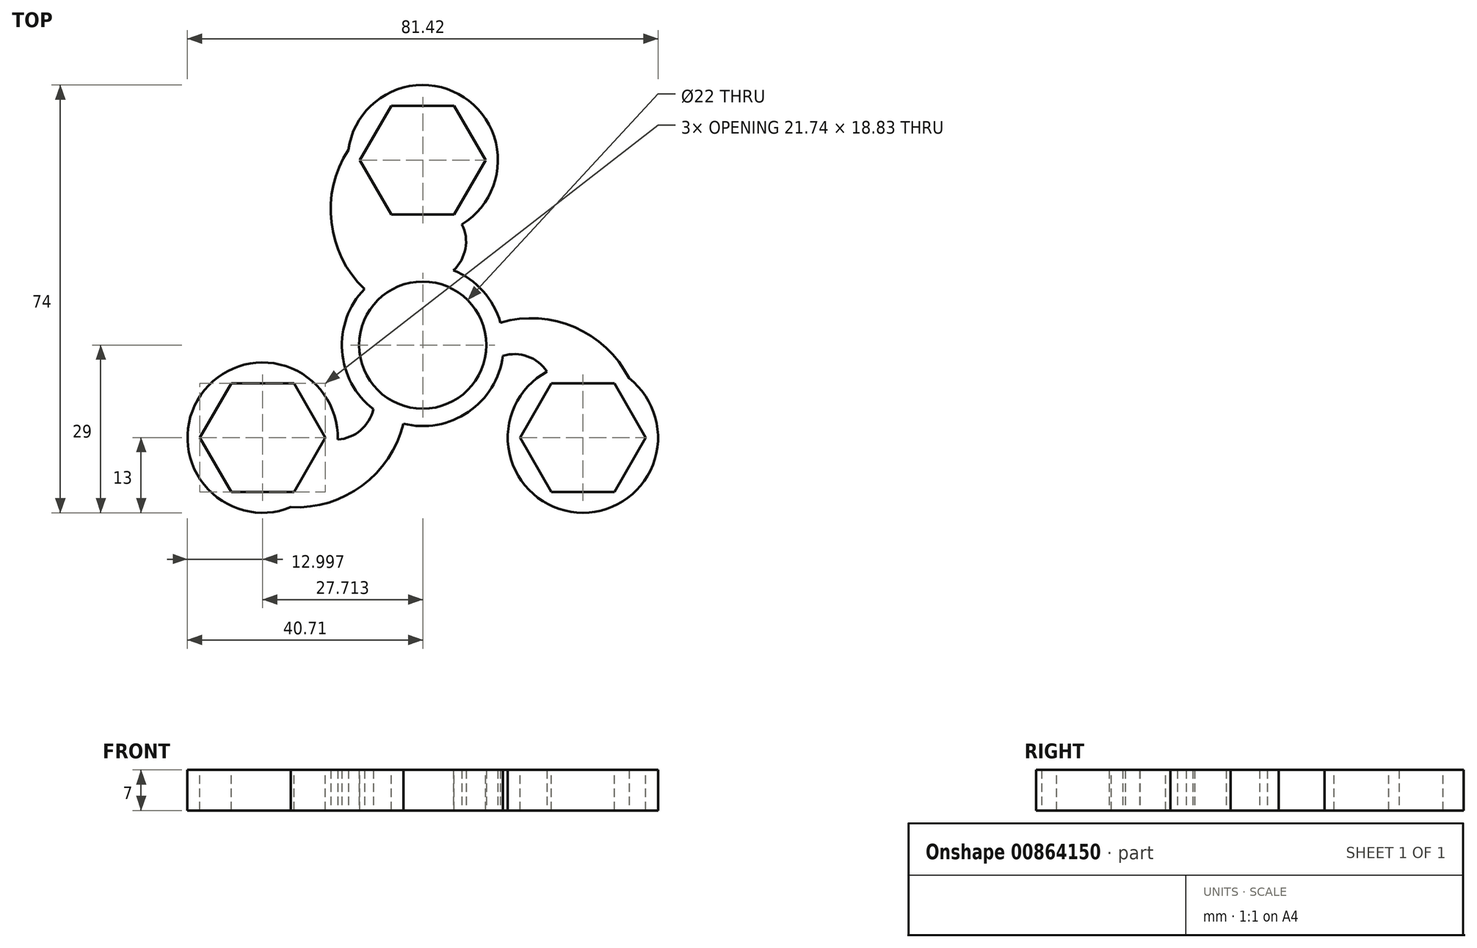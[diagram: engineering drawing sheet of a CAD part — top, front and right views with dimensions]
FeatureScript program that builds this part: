
annotation { "Feature Type Name" : "Feature", "Feature Type Description" : "" }
export const myFeature = defineFeature(function(context is Context, id is Id, definition is map)
    precondition{}
    {
        {
            var Q0;
            Q0=qCreatedBy(makeId("Top.planeOp"),FACE);
            var sketch = newSketch(context, id + "F0", { "sketchPlane" : qUnion([Q0])});
            skCircle(sketch, "E0", {"center": v(0, 0) * mm, "radius": 11 * mm});
            skCircle(sketch, "E1.0", {"center": v(0, 0) * mm, "radius": 14 * mm});
            skCircle(sketch, "E2", {"center": v(0, 0) * mm, "radius": 45 * mm, "construction": true});
            skCircle(sketch, "E3", {"center": v(0, 32) * mm, "radius": 13 * mm});
            skArc(sketch, "E4", {"start": v(-12.88, 33.78) * mm, "mid": v(-15.81, 21.24) * mm, "end": v(-10.1, 9.7) * mm});
            skArc(sketch, "E5", {"start": v(-6.79, 20.91) * mm, "mid": v(-7.38, 16.69) * mm, "end": v(-5.32, 12.95) * mm});
            skArc(sketch, "E6.MirrorCS", {"start": v(6.79, 20.91) * mm, "mid": v(7.38, 16.69) * mm, "end": v(5.32, 12.95) * mm});
            skArc(sketch, "E7.MirrorCS", {"start": v(12.88, 33.78) * mm, "mid": v(15.81, 21.24) * mm, "end": v(10.1, 9.7) * mm});
            skCircle(sketch, "E8.1.0", {"center": v(-27.71, -16) * mm, "radius": 13 * mm});
            skArc(sketch, "E8.1.1", {"start": v(-14.72, -16.33) * mm, "mid": v(-10.76, -14.73) * mm, "end": v(-8.55, -11.08) * mm});
            skArc(sketch, "E8.1.2", {"start": v(-22.81, -28.04) * mm, "mid": v(-10.49, -24.31) * mm, "end": v(-3.35, -13.6) * mm});
            skArc(sketch, "E8.1.3", {"start": v(-35.7, -5.74) * mm, "mid": v(-26.3, 3.07) * mm, "end": v(-13.45, 3.9) * mm});
            skArc(sketch, "E8.1.4", {"start": v(-21.5, -4.58) * mm, "mid": v(-18.14, -1.95) * mm, "end": v(-13.88, -1.87) * mm});
            skCircle(sketch, "E8.2.0", {"center": v(27.71, -16) * mm, "radius": 13 * mm});
            skArc(sketch, "E8.2.1", {"start": v(21.5, -4.58) * mm, "mid": v(18.14, -1.95) * mm, "end": v(13.88, -1.87) * mm});
            skArc(sketch, "E8.2.2", {"start": v(35.7, -5.74) * mm, "mid": v(26.3, 3.07) * mm, "end": v(13.45, 3.9) * mm});
            skArc(sketch, "E8.2.3", {"start": v(22.81, -28.04) * mm, "mid": v(10.49, -24.31) * mm, "end": v(3.35, -13.6) * mm});
            skArc(sketch, "E8.2.4", {"start": v(14.72, -16.33) * mm, "mid": v(10.76, -14.73) * mm, "end": v(8.55, -11.08) * mm});
            skSolve(sketch);
        }
        {
            var Q0;
            {var subQ0=sQuery(id+"F0.wireOp",EDGE,"E8.1.0");var subQ1=makeQuery(id+"F0.imprint","INTERSECT",VERTEX,{"derivedFrom":[subQ0,sQuery(id+"F0.wireOp",EDGE,"E8.1.2")]});Q0=makeQuery(id+"F0.imprint","IMPRINT",FACE,{"disambiguationData":[TD([[makeQuery(id+"F0.imprint","IMPRINT",EDGE,{"disambiguationData":[TD([[subQ1,1.0]])],"derivedFrom":subQ0}),1.0]])]});}
            var Q1;
            {var subQ0=sQuery(id+"F0.wireOp",EDGE,"E8.1.3");Q1=makeQuery(id+"F0.imprint","IMPRINT",FACE,{"disambiguationData":[TD([[makeQuery(id+"F0.imprint","IMPRINT",EDGE,{"derivedFrom":subQ0}),-1.0]])]});}
            var Q2;
            {var subQ0=sQuery(id+"F0.wireOp",EDGE,"E8.1.1");Q2=makeQuery(id+"F0.imprint","IMPRINT",FACE,{"disambiguationData":[TD([[makeQuery(id+"F0.imprint","IMPRINT",EDGE,{"derivedFrom":subQ0}),-1.0]])]});}
            var Q3;
            Q3=makeQuery(id+"F0.imprint","IMPRINT",FACE,{"disambiguationData":[TD([[makeQuery(id+"F0.imprint","IMPRINT",EDGE,{"derivedFrom":sQuery(id+"F0.wireOp",EDGE,"E0")}),-1.0]])]});
            var Q4;
            {var subQ0=sQuery(id+"F0.wireOp",EDGE,"E4");Q4=makeQuery(id+"F0.imprint","IMPRINT",FACE,{"disambiguationData":[TD([[makeQuery(id+"F0.imprint","IMPRINT",EDGE,{"derivedFrom":subQ0}),1.0]])]});}
            var Q5;
            {var subQ0=sQuery(id+"F0.wireOp",EDGE,"E3");var subQ1=makeQuery(id+"F0.imprint","INTERSECT",VERTEX,{"derivedFrom":[subQ0,sQuery(id+"F0.wireOp",EDGE,"E4")]});Q5=makeQuery(id+"F0.imprint","IMPRINT",FACE,{"disambiguationData":[TD([[makeQuery(id+"F0.imprint","IMPRINT",EDGE,{"disambiguationData":[TD([[subQ1,1.0]])],"derivedFrom":subQ0}),1.0]])]});}
            var Q6;
            {var subQ0=sQuery(id+"F0.wireOp",EDGE,"E6.MirrorCS");Q6=makeQuery(id+"F0.imprint","IMPRINT",FACE,{"disambiguationData":[TD([[makeQuery(id+"F0.imprint","IMPRINT",EDGE,{"derivedFrom":subQ0}),1.0]])]});}
            var Q7;
            {var subQ0=sQuery(id+"F0.wireOp",EDGE,"E8.2.1");Q7=makeQuery(id+"F0.imprint","IMPRINT",FACE,{"disambiguationData":[TD([[makeQuery(id+"F0.imprint","IMPRINT",EDGE,{"derivedFrom":subQ0}),-1.0]])]});}
            var Q8;
            {var subQ0=sQuery(id+"F0.wireOp",EDGE,"E8.2.3");Q8=makeQuery(id+"F0.imprint","IMPRINT",FACE,{"disambiguationData":[TD([[makeQuery(id+"F0.imprint","IMPRINT",EDGE,{"derivedFrom":subQ0}),-1.0]])]});}
            var Q9;
            {var subQ0=sQuery(id+"F0.wireOp",EDGE,"E8.2.0");var subQ1=makeQuery(id+"F0.imprint","INTERSECT",VERTEX,{"derivedFrom":[subQ0,sQuery(id+"F0.wireOp",EDGE,"E8.2.2")]});Q9=makeQuery(id+"F0.imprint","IMPRINT",FACE,{"disambiguationData":[TD([[makeQuery(id+"F0.imprint","IMPRINT",EDGE,{"disambiguationData":[TD([[subQ1,1.0]])],"derivedFrom":subQ0}),1.0]])]});}
            extrude(context, id + "F1", {"entities" : qUnion([Q0, Q1, Q2, Q3, Q4, Q5, Q6, Q7, Q8, Q9]), "depth" : 7 * mm, "offsetDistance" : 25 * mm});
        }
        {
            var Q0;
            Q0=makeQuery(id+"F1.opExtrude","CAP_FACE",FACE,{"disambiguationData":[OSD([sQuery(id+"F0.wireOp",EDGE,"E0"),sQuery(id+"F0.wireOp",EDGE,"E1.0"),sQuery(id+"F0.wireOp",EDGE,"E3"),sQuery(id+"F0.wireOp",EDGE,"E4"),sQuery(id+"F0.wireOp",EDGE,"E5"),sQuery(id+"F0.wireOp",EDGE,"E6.MirrorCS"),sQuery(id+"F0.wireOp",EDGE,"E7.MirrorCS"),sQuery(id+"F0.wireOp",EDGE,"E8.1.0"),sQuery(id+"F0.wireOp",EDGE,"E8.1.1"),sQuery(id+"F0.wireOp",EDGE,"E8.1.2"),sQuery(id+"F0.wireOp",EDGE,"E8.1.3"),sQuery(id+"F0.wireOp",EDGE,"E8.1.4"),sQuery(id+"F0.wireOp",EDGE,"E8.2.0"),sQuery(id+"F0.wireOp",EDGE,"E8.2.1"),sQuery(id+"F0.wireOp",EDGE,"E8.2.2"),sQuery(id+"F0.wireOp",EDGE,"E8.2.3"),sQuery(id+"F0.wireOp",EDGE,"E8.2.4")])],"isStart":false});
            var sketch = newSketch(context, id + "F2", { "sketchPlane" : qUnion([Q0])});
            skCircle(sketch, "E9.cCircle", {"center": v(0, 32) * mm, "radius": 9.41 * mm, "construction": true});
            skLineSegment(sketch, "E9.0", {"start": v(-5.44, 41.41) * mm, "end": v(5.44, 41.41) * mm});
            skLineSegment(sketch, "E9.1", {"start": v(5.44, 41.41) * mm, "end": v(10.87, 32) * mm});
            skLineSegment(sketch, "E9.2", {"start": v(10.87, 32) * mm, "end": v(5.44, 22.59) * mm});
            skLineSegment(sketch, "E9.3", {"start": v(5.44, 22.59) * mm, "end": v(-5.44, 22.59) * mm});
            skLineSegment(sketch, "E9.4", {"start": v(-5.44, 22.58) * mm, "end": v(-10.87, 32) * mm});
            skLineSegment(sketch, "E9.5", {"start": v(-10.87, 32) * mm, "end": v(-5.44, 41.41) * mm});
            skPoint(sketch, "E9.0.midPoint", {"position": v(0, 41.41) * mm});
            skLineSegment(sketch, "E10.1.0", {"start": v(-33.15, -25.41) * mm, "end": v(-38.58, -16) * mm});
            skLineSegment(sketch, "E10.1.1", {"start": v(-38.58, -16) * mm, "end": v(-33.15, -6.58) * mm});
            skLineSegment(sketch, "E10.1.2", {"start": v(-33.15, -6.58) * mm, "end": v(-22.28, -6.58) * mm});
            skLineSegment(sketch, "E10.1.3", {"start": v(-22.28, -6.58) * mm, "end": v(-16.84, -16) * mm});
            skLineSegment(sketch, "E10.1.4", {"start": v(-16.84, -16) * mm, "end": v(-22.28, -25.41) * mm});
            skLineSegment(sketch, "E10.1.5", {"start": v(-22.28, -25.41) * mm, "end": v(-33.15, -25.41) * mm});
            skCircle(sketch, "E10.1.6", {"center": v(-27.71, -16) * mm, "radius": 9.41 * mm, "construction": true});
            skLineSegment(sketch, "E10.2.0", {"start": v(38.58, -16) * mm, "end": v(33.15, -25.42) * mm});
            skLineSegment(sketch, "E10.2.1", {"start": v(33.15, -25.42) * mm, "end": v(22.28, -25.42) * mm});
            skLineSegment(sketch, "E10.2.2", {"start": v(22.28, -25.42) * mm, "end": v(16.84, -16) * mm});
            skLineSegment(sketch, "E10.2.3", {"start": v(16.84, -16) * mm, "end": v(22.28, -6.59) * mm});
            skLineSegment(sketch, "E10.2.4", {"start": v(22.28, -6.59) * mm, "end": v(33.15, -6.59) * mm});
            skLineSegment(sketch, "E10.2.5", {"start": v(33.15, -6.59) * mm, "end": v(38.58, -16) * mm});
            skCircle(sketch, "E10.2.6", {"center": v(27.71, -16) * mm, "radius": 9.41 * mm, "construction": true});
            skPoint(sketch, "E10.center", {"position": v(0, 0) * mm});
            skSolve(sketch);
        }
        {
            var Q0;
            Q0=makeQuery(id+"F2.imprint","IMPRINT",FACE,{"disambiguationData":[TD([[makeQuery(id+"F2.imprint","IMPRINT",EDGE,{"derivedFrom":sQuery(id+"F2.wireOp",EDGE,"E10.1.0")}),-1.0]])]});
            var Q1;
            Q1=makeQuery(id+"F2.imprint","IMPRINT",FACE,{"disambiguationData":[TD([[makeQuery(id+"F2.imprint","IMPRINT",EDGE,{"derivedFrom":sQuery(id+"F2.wireOp",EDGE,"E10.2.0")}),-1.0]])]});
            var Q2;
            Q2=makeQuery(id+"F2.imprint","IMPRINT",FACE,{"disambiguationData":[TD([[makeQuery(id+"F2.imprint","IMPRINT",EDGE,{"derivedFrom":sQuery(id+"F2.wireOp",EDGE,"E9.0")}),-1.0]])]});
            extrude(context, id + "F3", {"entities" : qUnion([Q0, Q1, Q2]), "operationType" : NewBodyOperationType.REMOVE, "oppositeDirection" : true, "depth" : 31 * mm, "offsetDistance" : 25 * mm});
        }
    });
